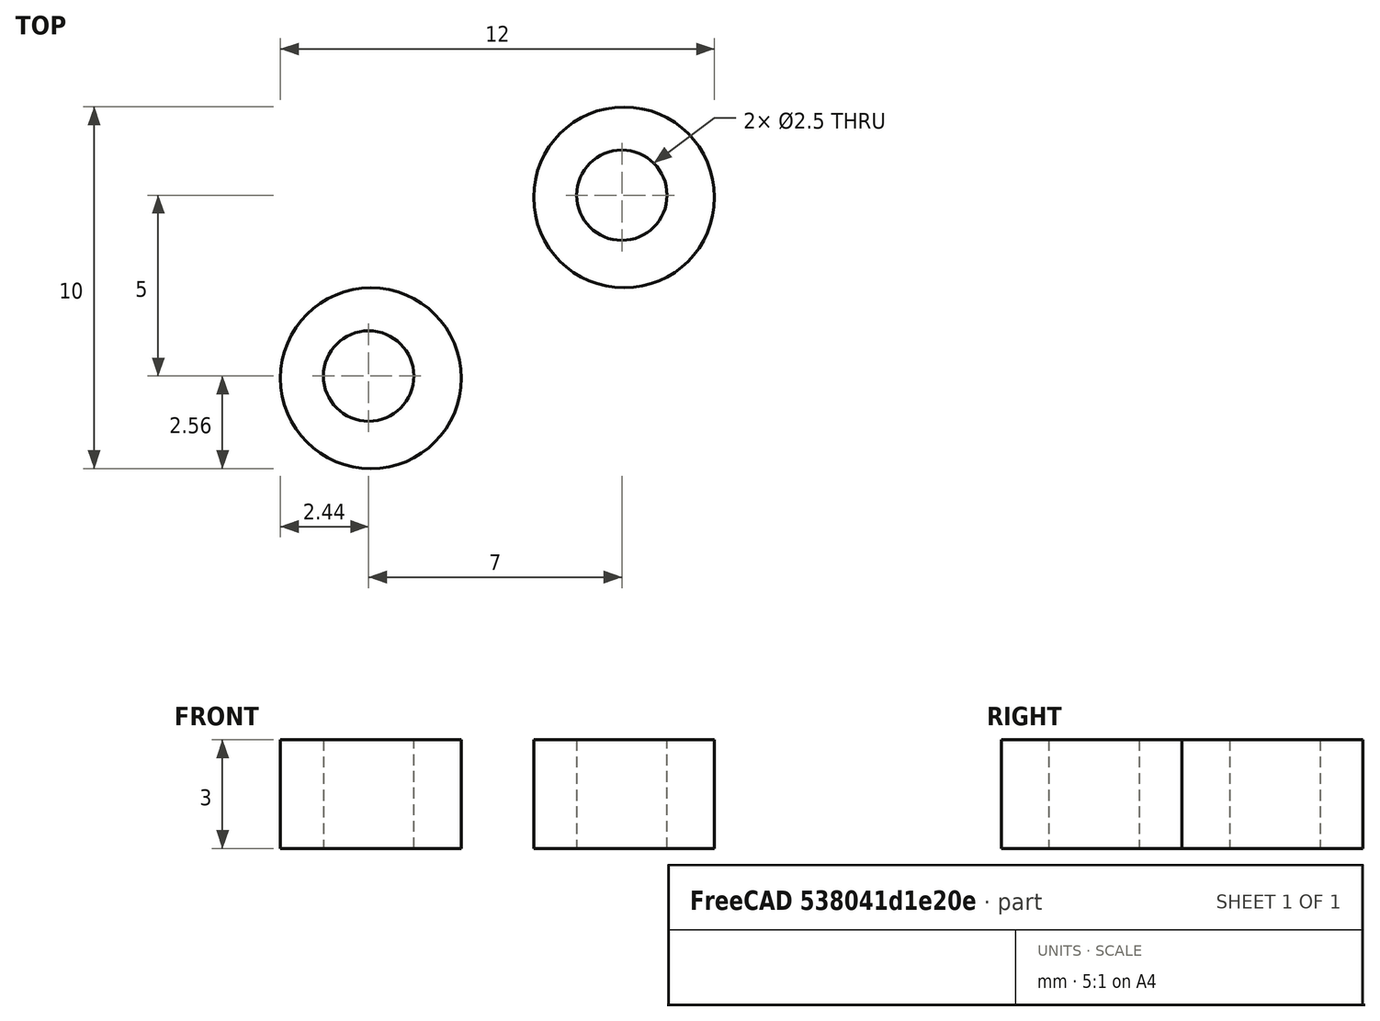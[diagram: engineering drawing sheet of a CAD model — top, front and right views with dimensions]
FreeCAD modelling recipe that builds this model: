
FCSTD DOCUMENT  (FreeCAD 0.18R16131 (Git))
Label: buteeRobot
License: All rights reserved
LicenseURL: http://en.wikipedia.org/wiki/All_rights_reserved
objects: PartDesign::Body×2, Sketcher::SketchObject×1, PartDesign::Pad×1, PartDesign::FeatureBase×1
note: 6 computed .brp shape members not serialized (recipe doc carries the construction recipe); baked Part::Feature solids carry a one-line shape summary decoded from their .brp

FEATURE [Sketcher::SketchObject] Sketch
  MapMode = 5
  Support = -> [XY_Plane]
  sketch-geometry (2):
    g0: Circle CenterX=0 CenterY=0 CenterZ=0 NormalX=0 NormalY=0 NormalZ=1 AngleXU=0 Radius=1.25
    g1: Circle CenterX=0.062527 CenterY=-0.062529 CenterZ=0 NormalX=0 NormalY=0 NormalZ=1 AngleXU=0 Radius=2.5
  constraints (3):
    c: Coincident(g0,g-1)
    c: Diameter(g1) = 5
    c: Diameter(g0) = 2.5
FEATURE [PartDesign::Pad] Pad
  Length = 3
  Length2 = 100
  Profile = -> Sketch
  Type = 0
FEATURE [PartDesign::Body] Body
  Group = -> [Sketch,Pad]
  Origin = -> Origin
  Tip = -> Pad
FEATURE [PartDesign::FeatureBase] Clone
  BaseFeature = -> Pad
  Placement = pos=(7,5,0) rot=(0,0,1;0rad)
FEATURE [PartDesign::Body] Body001
  Group = -> [Clone]
  Origin = -> Origin001
  Tip = -> Clone
